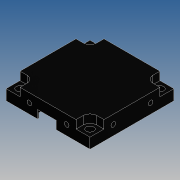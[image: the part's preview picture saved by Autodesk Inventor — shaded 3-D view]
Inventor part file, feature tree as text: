
AUTODESK INVENTOR PART (.ipt)
format: ipt  version: 2019 (Build 230136000, 136)  size: 299,520 bytes
history: native  units: mm
features: sketch x6, extrude x4, hole x2, plane x1, mirror x1, pattern_circular x1
ambient origin geometry x8: Origin, YZ Plane, XZ Plane, XY Plane, X Axis, Y Axis, Z Axis, Center Point
bodies: Solid1 (feature_tree)
feature tree (15):
  extrude  "Extrusion1"  Depth=18.0mm
  hole  "Hole1"  [1 undecoded]
  extrude  "Extrusion2"  Depth=3.0mm
  extrude  "Extrusion3"  Depth=3.5mm TaperAngle=360.0deg
  hole  "M3/6/10"  [1 undecoded]
  plane  "Work Plane1"
  mirror  "Mirror1"
  pattern_circular  "Circular Pattern1"  [2 undecoded]
  extrude  "Extrusion4"  Depth=2.0mm TaperAngle=0.0deg
  sketch  "Sketch1"  dims[d0=18.0mm d1=18.0mm]
  sketch  "Sketch2"  dims[d2=8.0mm d3=0.0mm d4=15.0mm]
  sketch  "Sketch3"  dims[d5=15.0mm]
  sketch  "Sketch4"  dims[d6=3.2mm d7=6.0mm d8=6.0mm d9=2.0mm d10=90.0deg d11=8.0mm d12=20.594885mm d13=3.0mm]
  sketch  "Sketch5"  dims[d14=3.5mm d15=0.0mm d16=40.0mm d17=360.0deg]
  sketch  "Sketch7"  dims[d19=0.5mm d20=0.5mm d21=3.0mm d22=2.0mm d23=0.0mm d24=8.0mm d25=3.8mm d26=2.0mm d27=6.0mm d28=6.0mm d29=2.0mm d30=90.0deg d31=2.0mm d32=0.0mm d33=9.0mm d34=8.0mm d35=2.0mm d36=18.5mm d37=3.5mm d38=0.0mm d39=1.0mm d40=1.0mm]
note: 4 required parameter values undecoded (feature->parameter linkage not recoverable at this tier; creation-order binding heuristic only, values carry confidence <= 0.55)
